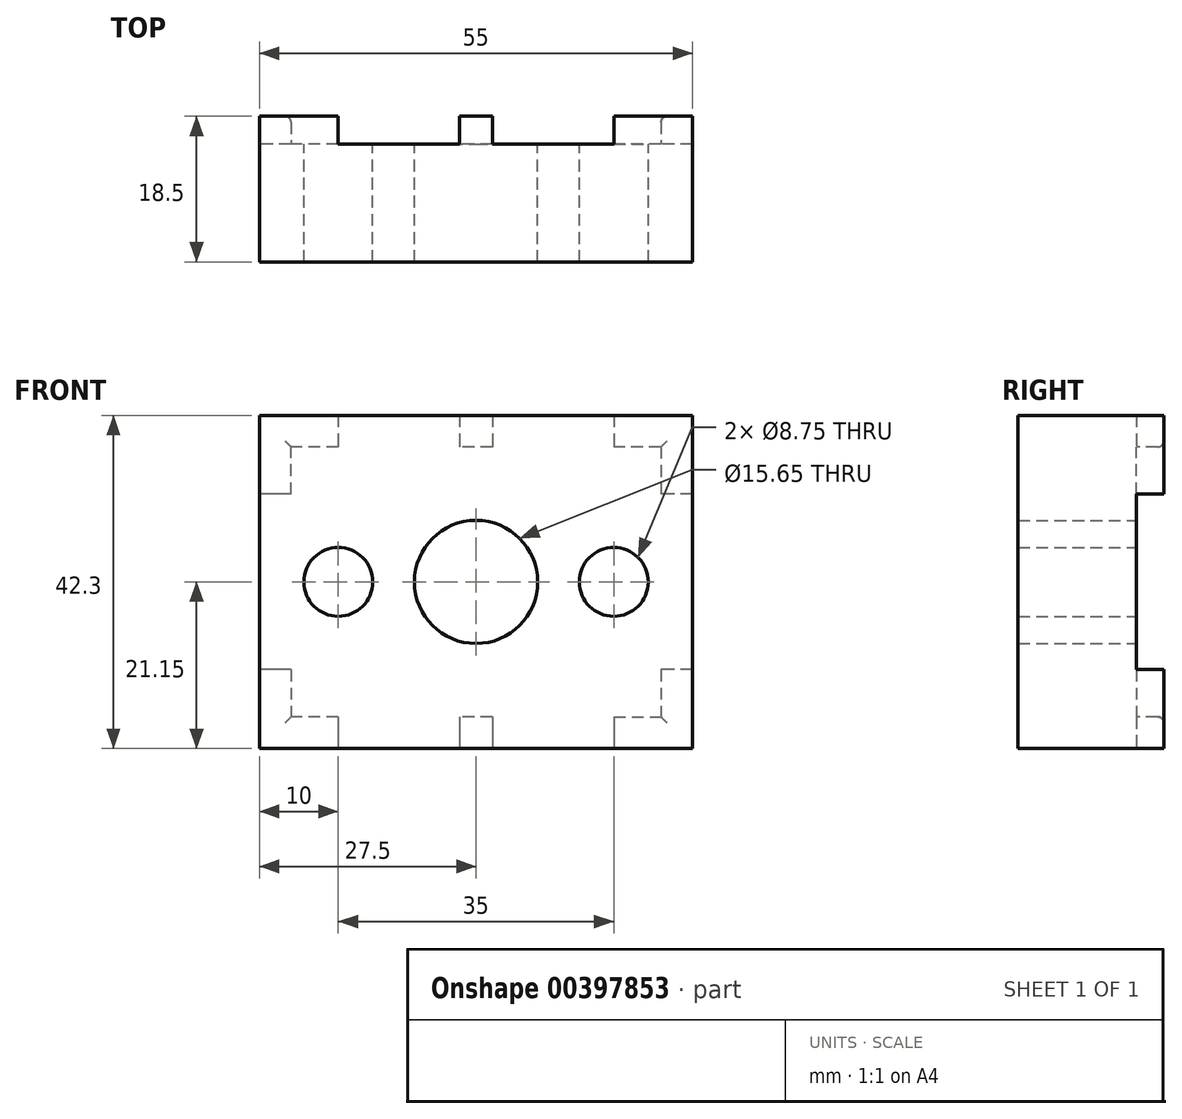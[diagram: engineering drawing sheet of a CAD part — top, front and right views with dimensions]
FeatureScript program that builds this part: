
annotation { "Feature Type Name" : "Feature", "Feature Type Description" : "" }
export const myFeature = defineFeature(function(context is Context, id is Id, definition is map)
    precondition{}
    {
        {
            var Q0;
            Q0=qCreatedBy(makeId("Front.planeOp"),FACE);
            var sketch = newSketch(context, id + "F0", { "sketchPlane" : qUnion([Q0])});
            skLineSegment(sketch, "E0.bottom", {"start": v(-27.5, 21.15) * mm, "end": v(27.5, 21.15) * mm});
            skLineSegment(sketch, "E0.top", {"start": v(-27.5, -21.15) * mm, "end": v(27.5, -21.15) * mm});
            skLineSegment(sketch, "E0.left", {"start": v(-27.5, 21.15) * mm, "end": v(-27.5, -21.15) * mm});
            skLineSegment(sketch, "E0.right", {"start": v(27.5, 21.15) * mm, "end": v(27.5, -21.15) * mm});
            skPoint(sketch, "E0.middle", {"position": v(0, 0) * mm});
            skCircle(sketch, "E1", {"center": v(0, 0) * mm, "radius": 7.83 * mm});
            skPoint(sketch, "E2", {"position": v(-17.5, 0) * mm});
            skPoint(sketch, "E3", {"position": v(17.5, 0) * mm});
            skCircle(sketch, "E4", {"center": v(-17.5, 0) * mm, "radius": 4.38 * mm});
            skCircle(sketch, "E5", {"center": v(17.5, 0) * mm, "radius": 4.38 * mm});
            skSolve(sketch);
        }
        {
            var Q0;
            Q0 = qSketchRegion(id + "F0", true);
            extrude(context, id + "F1", {"entities" : qUnion([Q0]), "depth" : 15 * mm});
        }
        {
            var Q0;
            Q0=makeQuery(id+"F1.opExtrude","CAP_FACE",FACE,{"disambiguationData":[OSD([sQuery(id+"F0.wireOp",EDGE,"E0.bottom"),sQuery(id+"F0.wireOp",EDGE,"E0.top"),sQuery(id+"F0.wireOp",EDGE,"E0.left"),sQuery(id+"F0.wireOp",EDGE,"E0.right"),sQuery(id+"F0.wireOp",EDGE,"E1"),sQuery(id+"F0.wireOp",EDGE,"E4"),sQuery(id+"F0.wireOp",EDGE,"E5")])],"isStart":true});
            var sketch = newSketch(context, id + "F2", { "sketchPlane" : qUnion([Q0])});
            skCircle(sketch, "E6", {"center": v(0, 0) * mm, "radius": 21.15 * mm, "construction": true});
            skPoint(sketch, "E7", {"position": v(0, 21.15) * mm});
            skPoint(sketch, "E8", {"position": v(0, -21.15) * mm});
            skLineSegment(sketch, "E9.bottom", {"start": v(-2.1, 25.15) * mm, "end": v(2.1, 25.15) * mm});
            skLineSegment(sketch, "E9.top", {"start": v(-2.1, 17.15) * mm, "end": v(2.1, 17.15) * mm});
            skLineSegment(sketch, "E9.left", {"start": v(-2.1, 25.15) * mm, "end": v(-2.1, 17.15) * mm});
            skLineSegment(sketch, "E9.right", {"start": v(2.1, 25.15) * mm, "end": v(2.1, 17.15) * mm});
            skLineSegment(sketch, "E10.bottom", {"start": v(-2.1, -17.15) * mm, "end": v(2.1, -17.15) * mm});
            skLineSegment(sketch, "E10.top", {"start": v(-2.1, -25.15) * mm, "end": v(2.1, -25.15) * mm});
            skLineSegment(sketch, "E10.left", {"start": v(-2.1, -17.15) * mm, "end": v(-2.1, -25.15) * mm});
            skLineSegment(sketch, "E10.right", {"start": v(2.1, -17.15) * mm, "end": v(2.1, -25.15) * mm});
            skLineSegment(sketch, "E11.bottom", {"start": v(-23.5, 17.15) * mm, "end": v(23.5, 17.15) * mm, "construction": true});
            skLineSegment(sketch, "E11.top", {"start": v(-23.5, -17.15) * mm, "end": v(23.5, -17.15) * mm, "construction": true});
            skLineSegment(sketch, "E11.left", {"start": v(-23.5, 17.15) * mm, "end": v(-23.5, -17.15) * mm, "construction": true});
            skLineSegment(sketch, "E11.right", {"start": v(23.5, 17.15) * mm, "end": v(23.5, -17.15) * mm, "construction": true});
            skLineSegment(sketch, "E12", {"start": v(-17.5, 21.15) * mm, "end": v(-17.5, 17.15) * mm});
            skLineSegment(sketch, "E13", {"start": v(-17.5, -17.15) * mm, "end": v(-17.5, -21.15) * mm});
            skLineSegment(sketch, "E14", {"start": v(17.5, 21.15) * mm, "end": v(17.5, 17.15) * mm});
            skLineSegment(sketch, "E15", {"start": v(17.5, -17.15) * mm, "end": v(17.5, -21.15) * mm});
            skLineSegment(sketch, "E16", {"start": v(-27.5, -11.15) * mm, "end": v(-23.5, -11.15) * mm});
            skLineSegment(sketch, "E17", {"start": v(23.5, -11.15) * mm, "end": v(27.5, -11.15) * mm});
            skLineSegment(sketch, "E18", {"start": v(-27.5, 11.15) * mm, "end": v(-23.5, 11.15) * mm});
            skLineSegment(sketch, "E19", {"start": v(23.5, 11.15) * mm, "end": v(27.5, 11.15) * mm});
            skLineSegment(sketch, "E20", {"start": v(17.5, 17.15) * mm, "end": v(23.5, 17.15) * mm});
            skLineSegment(sketch, "E21", {"start": v(23.5, 11.15) * mm, "end": v(23.5, 17.15) * mm});
            skLineSegment(sketch, "E22", {"start": v(23.5, -11.15) * mm, "end": v(23.5, -17.15) * mm});
            skLineSegment(sketch, "E23", {"start": v(17.5, -17.15) * mm, "end": v(23.5, -17.15) * mm});
            skLineSegment(sketch, "E24", {"start": v(-17.5, -17.15) * mm, "end": v(-23.5, -17.15) * mm});
            skLineSegment(sketch, "E25", {"start": v(-23.5, -11.15) * mm, "end": v(-23.5, -17.15) * mm});
            skLineSegment(sketch, "E26", {"start": v(-23.5, 17.15) * mm, "end": v(-23.5, 11.15) * mm});
            skLineSegment(sketch, "E27", {"start": v(-23.5, 17.15) * mm, "end": v(-17.5, 17.15) * mm});
            skLineSegment(sketch, "E28", {"start": v(17.5, 21.15) * mm, "end": v(27.5, 21.15) * mm});
            skLineSegment(sketch, "E29", {"start": v(27.5, 21.15) * mm, "end": v(27.5, 11.15) * mm});
            skLineSegment(sketch, "E30", {"start": v(27.5, -11.15) * mm, "end": v(27.5, -21.15) * mm});
            skLineSegment(sketch, "E31", {"start": v(27.5, -21.15) * mm, "end": v(17.5, -21.15) * mm});
            skLineSegment(sketch, "E32", {"start": v(-17.5, -21.15) * mm, "end": v(-27.5, -21.15) * mm});
            skLineSegment(sketch, "E33", {"start": v(-27.5, -21.15) * mm, "end": v(-27.5, -11.15) * mm});
            skLineSegment(sketch, "E34", {"start": v(-27.5, 11.15) * mm, "end": v(-27.5, 21.15) * mm});
            skLineSegment(sketch, "E35", {"start": v(-27.5, 21.15) * mm, "end": v(-17.5, 21.15) * mm});
            skSolve(sketch);
        }
        {
            var Q0;
            {var subQ0=sQuery(id+"F2.wireOp",EDGE,"E9.top");Q0=makeQuery(id+"F2.imprint","IMPRINT",FACE,{"disambiguationData":[TD([[makeQuery(id+"F2.imprint","IMPRINT",EDGE,{"derivedFrom":subQ0}),1.0]])]});}
            var Q1;
            {var subQ0=sQuery(id+"F2.wireOp",EDGE,"E10.bottom");Q1=makeQuery(id+"F2.imprint","IMPRINT",FACE,{"disambiguationData":[TD([[makeQuery(id+"F2.imprint","IMPRINT",EDGE,{"derivedFrom":subQ0}),-1.0]])]});}
            var Q2;
            Q2=makeQuery(id+"F2.imprint","IMPRINT",FACE,{"disambiguationData":[TD([[makeQuery(id+"F2.imprint","IMPRINT",EDGE,{"derivedFrom":sQuery(id+"F2.wireOp",EDGE,"E12")}),-1.0]])]});
            var Q3;
            Q3=makeQuery(id+"F2.imprint","IMPRINT",FACE,{"disambiguationData":[TD([[makeQuery(id+"F2.imprint","IMPRINT",EDGE,{"derivedFrom":sQuery(id+"F2.wireOp",EDGE,"E13")}),-1.0]])]});
            var Q4;
            Q4=makeQuery(id+"F2.imprint","IMPRINT",FACE,{"disambiguationData":[TD([[makeQuery(id+"F2.imprint","IMPRINT",EDGE,{"derivedFrom":sQuery(id+"F2.wireOp",EDGE,"E14")}),1.0]])]});
            var Q5;
            Q5=makeQuery(id+"F2.imprint","IMPRINT",FACE,{"disambiguationData":[TD([[makeQuery(id+"F2.imprint","IMPRINT",EDGE,{"derivedFrom":sQuery(id+"F2.wireOp",EDGE,"E15")}),1.0]])]});
            extrude(context, id + "F3", {"entities" : qUnion([Q0, Q1, Q2, Q3, Q4, Q5]), "operationType" : NewBodyOperationType.ADD, "depth" : 3.5 * mm});
        }
        {
            var Q0;
            Q0=makeQuery(id+"F3.opExtrude","CAP_EDGE",EDGE,{"disambiguationData":[OSD([sQuery(id+"F2.wireOp",EDGE,"E10.bottom")])],"isStart":false});
            var Q1;
            Q1=makeQuery(id+"F3.opExtrude","CAP_EDGE",EDGE,{"disambiguationData":[OSD([sQuery(id+"F2.wireOp",EDGE,"E9.top")])],"isStart":false});
            var Q2;
            Q2=makeQuery(id+"F3.opExtrude","CAP_EDGE",EDGE,{"disambiguationData":[OSD([sQuery(id+"F2.wireOp",EDGE,"E27")])],"isStart":false});
            var Q3;
            Q3=makeQuery(id+"F3.opExtrude","CAP_EDGE",EDGE,{"disambiguationData":[OSD([sQuery(id+"F2.wireOp",EDGE,"E26")])],"isStart":false});
            var Q4;
            Q4=makeQuery(id+"F3.opExtrude","CAP_EDGE",EDGE,{"disambiguationData":[OSD([sQuery(id+"F2.wireOp",EDGE,"E25")])],"isStart":false});
            var Q5;
            Q5=makeQuery(id+"F3.opExtrude","CAP_EDGE",EDGE,{"disambiguationData":[OSD([sQuery(id+"F2.wireOp",EDGE,"E24")])],"isStart":false});
            var Q6;
            Q6=makeQuery(id+"F3.opExtrude","CAP_EDGE",EDGE,{"disambiguationData":[OSD([sQuery(id+"F2.wireOp",EDGE,"E23")])],"isStart":false});
            var Q7;
            Q7=makeQuery(id+"F3.opExtrude","CAP_EDGE",EDGE,{"disambiguationData":[OSD([sQuery(id+"F2.wireOp",EDGE,"E22")])],"isStart":false});
            var Q8;
            Q8=makeQuery(id+"F3.opExtrude","CAP_EDGE",EDGE,{"disambiguationData":[OSD([sQuery(id+"F2.wireOp",EDGE,"E21")])],"isStart":false});
            var Q9;
            Q9=makeQuery(id+"F3.opExtrude","CAP_EDGE",EDGE,{"disambiguationData":[OSD([sQuery(id+"F2.wireOp",EDGE,"E20")])],"isStart":false});
            fillet(context, id + "F4", {"entities" : qUnion([Q0, Q1, Q2, Q3, Q4, Q5, Q6, Q7, Q8, Q9]), "radius" : 0.75 * mm, "tangentPropagation" : true, "allowEdgeOverflow" : false});
        }
    });
